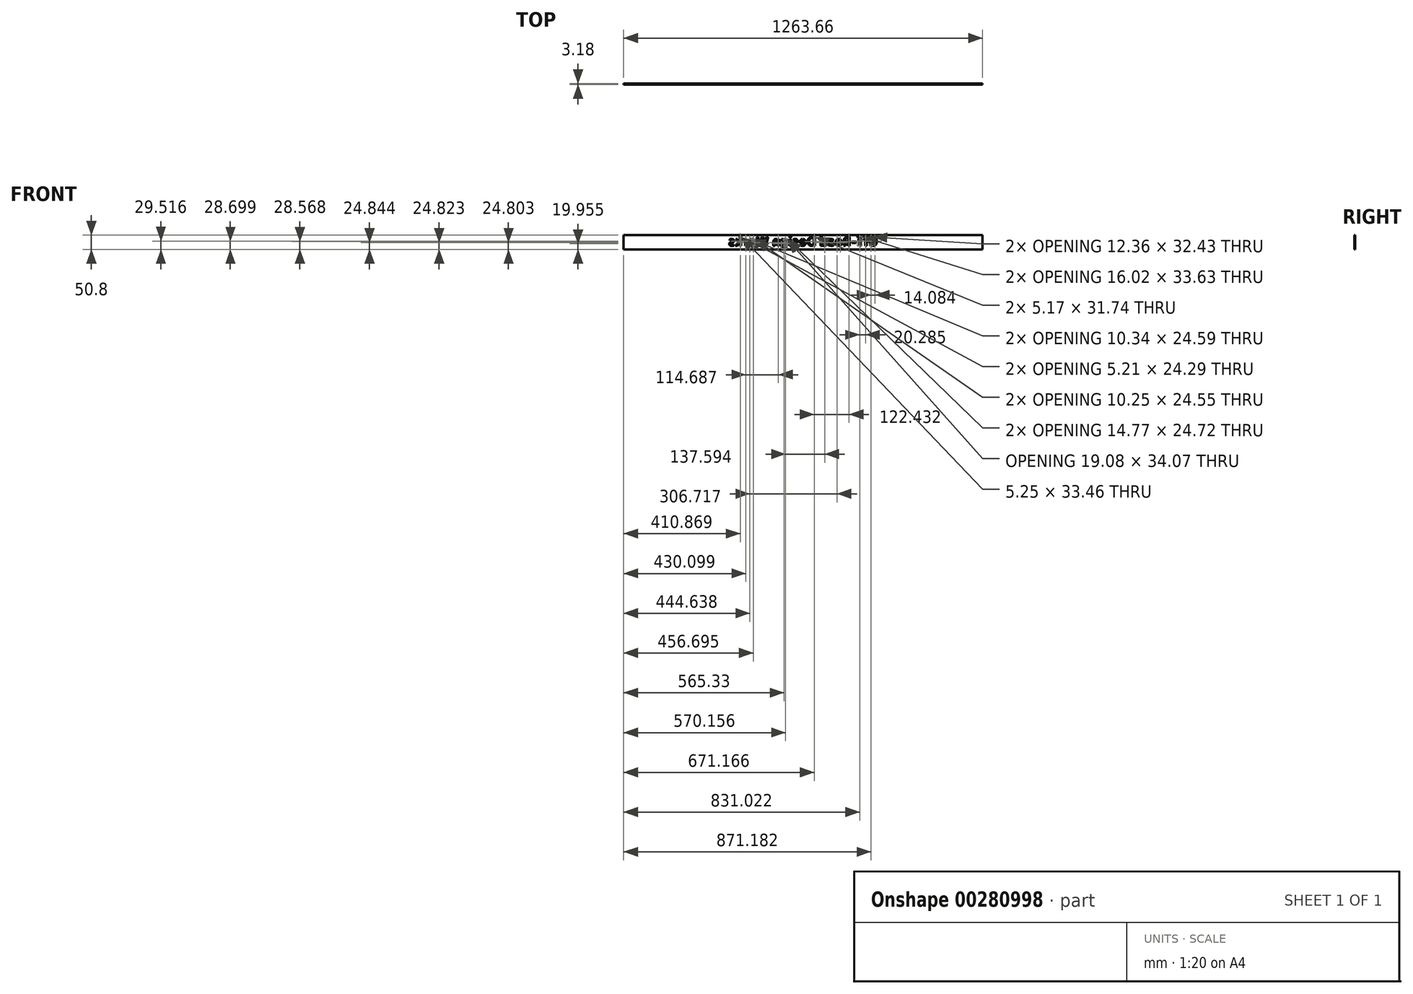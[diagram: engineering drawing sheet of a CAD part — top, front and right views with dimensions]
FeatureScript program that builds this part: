
annotation { "Feature Type Name" : "Feature", "Feature Type Description" : "" }
export const myFeature = defineFeature(function(context is Context, id is Id, definition is map)
    precondition{}
    {
        {
            var Q0;
            Q0=qCreatedBy(makeId("Right.planeOp"),FACE);
            var sketch = newSketch(context, id + "F0", { "sketchPlane" : qUnion([Q0])});
            skLineSegment(sketch, "E0.bottom", {"start": v(1.59, -25.4) * mm, "end": v(-1.59, -25.4) * mm});
            skLineSegment(sketch, "E0.top", {"start": v(1.59, 25.4) * mm, "end": v(-1.59, 25.4) * mm});
            skLineSegment(sketch, "E0.left", {"start": v(1.59, -25.4) * mm, "end": v(1.59, 25.4) * mm});
            skLineSegment(sketch, "E0.right", {"start": v(-1.59, -25.4) * mm, "end": v(-1.59, 25.4) * mm});
            skPoint(sketch, "E0.middle", {"position": v(0, 0) * mm});
            skSolve(sketch);
        }
        {
            var Q0;
            Q0 = qSketchRegion(id + "F0", true);
            extrude(context, id + "F1", {"entities" : qUnion([Q0]), "endBound" : BoundingType.SYMMETRIC, "depth" : 1263.65 * mm});
        }
        {
            var Q0;
            Q0=makeQuery(id+"F1.opExtrude","SWEPT_FACE",FACE,{"disambiguationData":[OSD([sQuery(id+"F0.wireOp",EDGE,"E0.left")])]});
            var sketch = newSketch(context, id + "F2", { "sketchPlane" : qUnion([Q0])});
            skText(sketch, "E1", { "text": "Off-Road Design Works", "fontName": "AllertaStencil-Regular.ttf"});
            skLineSegment(sketch, "E2", {"start": v(0, -12.7) * mm, "end": v(0, 0) * mm, "construction": true});
            const initialGuessF2  = {"E1": [-0.26293, -0.0127, 1, 0, 0.03175]};
            skSetInitialGuess(sketch, initialGuessF2);
            skSolve(sketch);
        }
        {
            var Q0;
            Q0 = qSketchRegion(id + "F2", true);
            var Q1;
            Q1=makeQuery(id+"F1.opExtrude","SWEPT_FACE",FACE,{"disambiguationData":[OSD([sQuery(id+"F0.wireOp",EDGE,"E0.right")])]});
            extrude(context, id + "F3", {"entities" : qUnion([Q0]), "operationType" : NewBodyOperationType.REMOVE, "endBound" : BoundingType.UP_TO_SURFACE, "oppositeDirection" : true, "endBoundEntityFace" : qUnion([Q1]), "depth" : 25.4 * mm});
        }
    });
